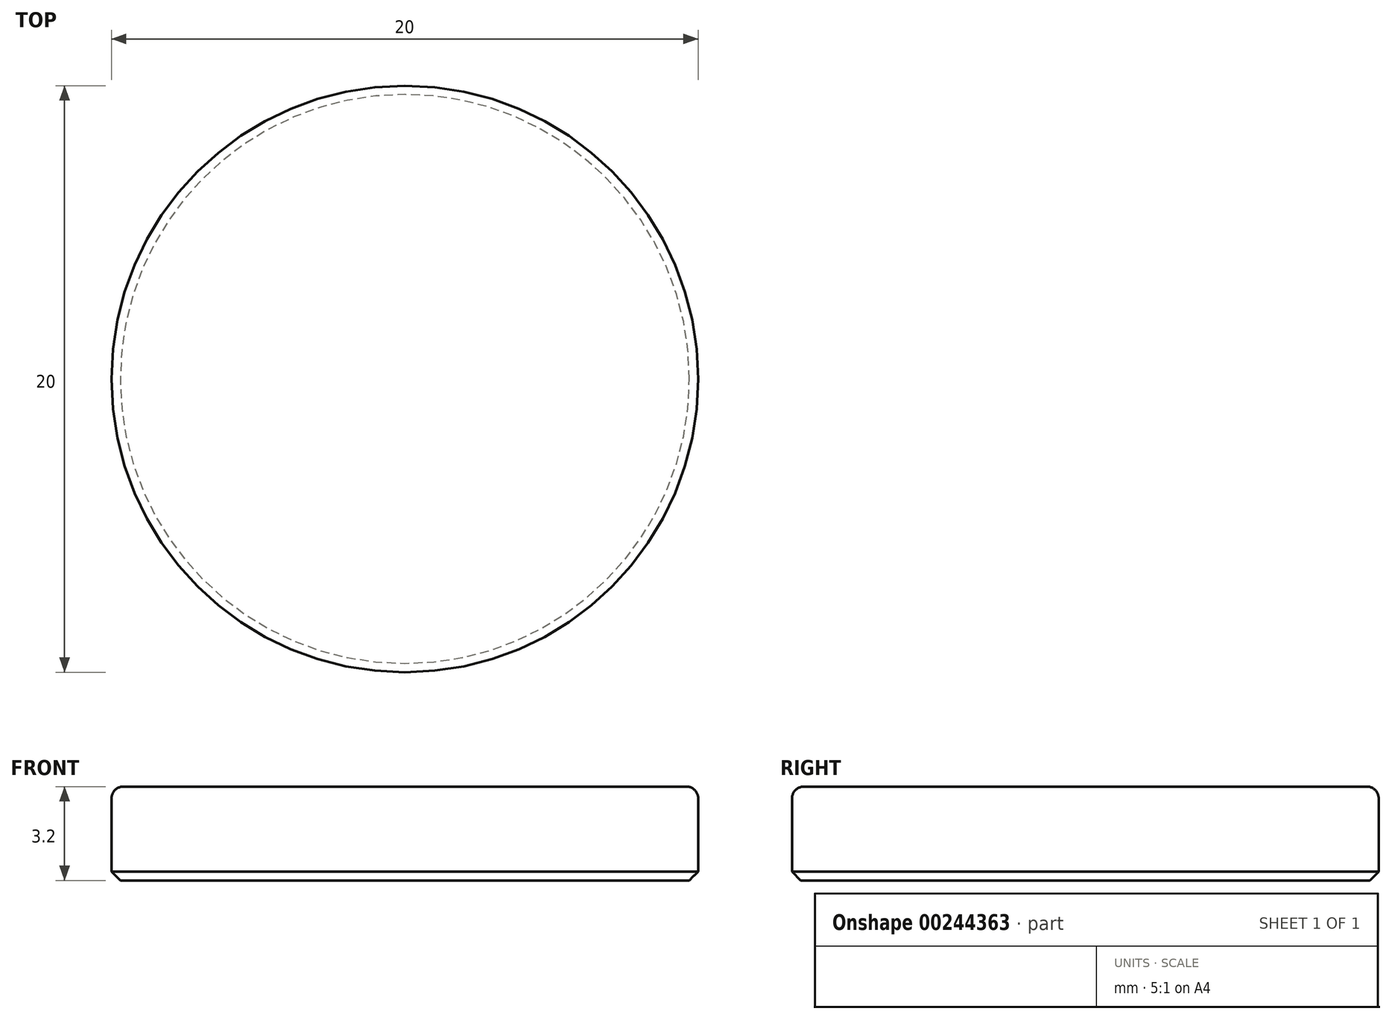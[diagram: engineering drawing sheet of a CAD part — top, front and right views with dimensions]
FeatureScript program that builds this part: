
annotation { "Feature Type Name" : "Feature", "Feature Type Description" : "" }
export const myFeature = defineFeature(function(context is Context, id is Id, definition is map)
    precondition{}
    {
        {
            var Q0;
            Q0=qCreatedBy(makeId("Top.planeOp"),FACE);
            var sketch = newSketch(context, id + "F0", { "sketchPlane" : qUnion([Q0])});
            skCircle(sketch, "E0", {"center": v(0, 0) * mm, "radius": 10 * mm});
            skSolve(sketch);
        }
        {
            var Q0;
            Q0 = qSketchRegion(id + "F0", true);
            extrude(context, id + "F1", {"entities" : qUnion([Q0]), "depth" : 3.2 * mm});
        }
        {
            var Q0;
            Q0=makeQuery(id+"F1.opExtrude","CAP_EDGE",EDGE,{"disambiguationData":[OSD([sQuery(id+"F0.wireOp",EDGE,"E0")])],"isStart":false});
            fillet(context, id + "F2", {"entities" : qUnion([Q0]), "radius" : .4 * mm, "tangentPropagation" : true, "allowEdgeOverflow" : false});
        }
        {
            var Q0;
            Q0=makeQuery(id+"F1.opExtrude","CAP_EDGE",EDGE,{"disambiguationData":[OSD([sQuery(id+"F0.wireOp",EDGE,"E0")])],"isStart":true});
            chamfer(context, id + "F3", {"entities" : qUnion([Q0]), "width" : .3 * mm, "tangentPropagation" : true});
        }
    });
